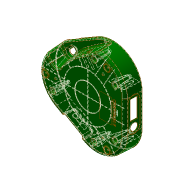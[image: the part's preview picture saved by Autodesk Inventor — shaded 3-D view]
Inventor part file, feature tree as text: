
AUTODESK INVENTOR PART (.ipt)
format: ipt  version: 2016 (Build 200138000, 138)  size: 3,062,272 bytes
history: native  units: in
note: dims shown in document units (in); Inventor stores cm internally (conversion verified against a paired STEP export)
features: reference x2, other x1, sketch x1, plane x1, extrude x1, fillet x1, imported_body x1
ambient origin geometry x8: Origin, YZ Plane, XZ Plane, XY Plane, X Axis, Y Axis, Z Axis, Center Point
bodies: Solid1 (feature_tree), Solid2 (feature_tree)
feature tree (8):
  other  "bottom_cover-2016-04-29-21"
  sketch  "Sketch1"  dims[d0=0.0709in d1=0.0709in d2=0.3543in d3=0.3543in d4=1.9685in d5=1.5748in d6=0.3937in d7=-0.0069in d8=0.1969in]
  plane  "Work Plane1"
  extrude  "Extrusion1"  Depth=0.1969in
  fillet  "Fillet1"  Radius=0.3543in
  imported_body  "Base1"
  reference  "Reference1"
  reference  "Reference2"
